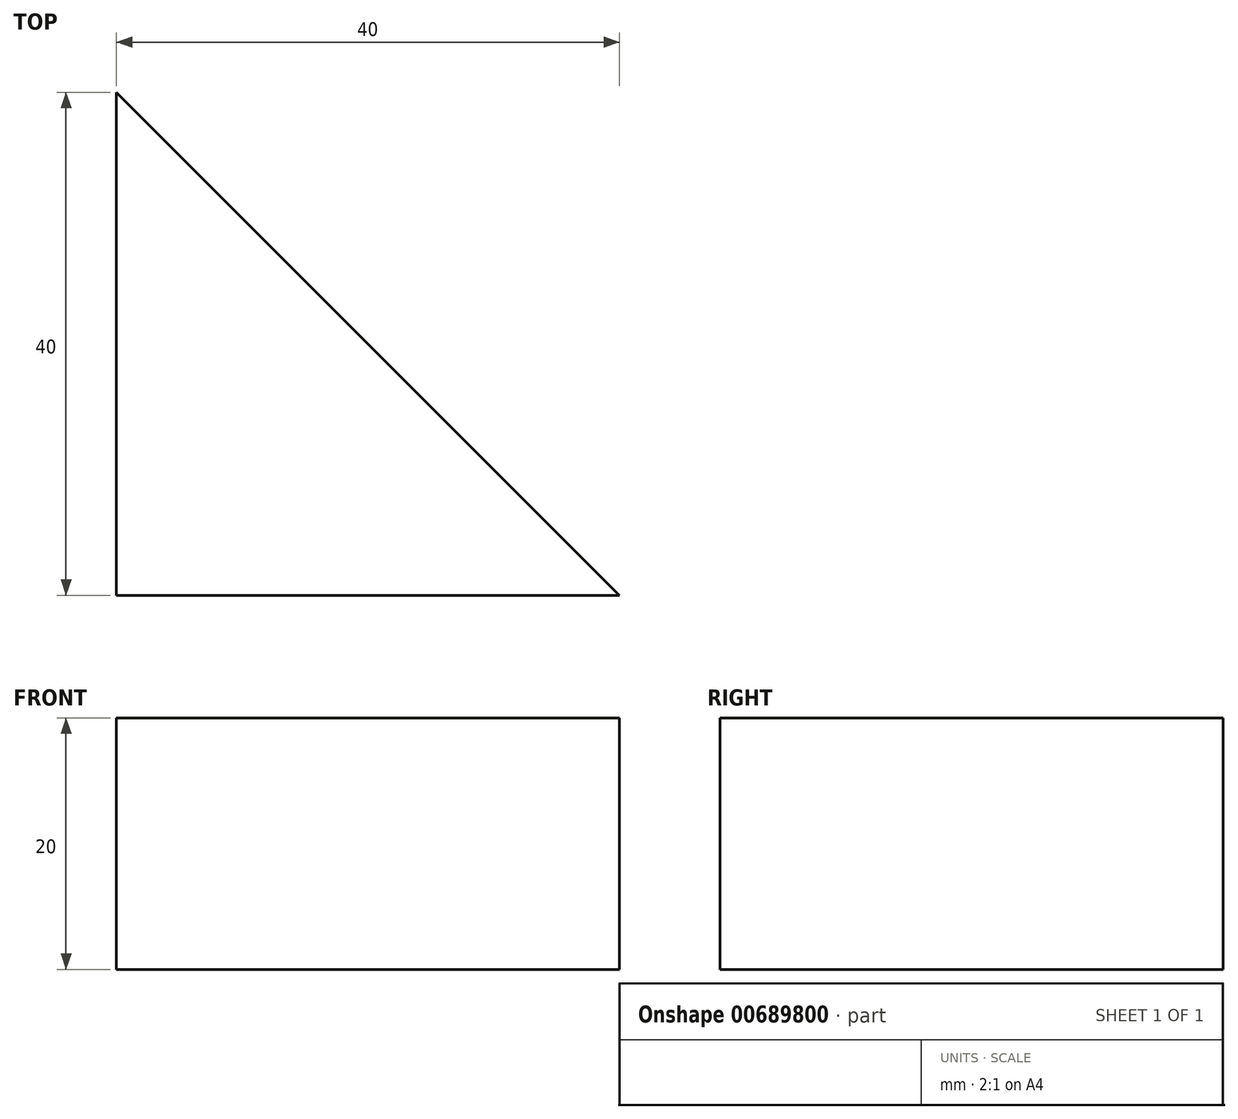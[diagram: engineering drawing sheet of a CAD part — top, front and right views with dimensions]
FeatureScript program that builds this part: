
annotation { "Feature Type Name" : "Feature", "Feature Type Description" : "" }
export const myFeature = defineFeature(function(context is Context, id is Id, definition is map)
    precondition{}
    {
        {
            var Q0;
            Q0=qCreatedBy(makeId("Top.planeOp"),FACE);
            var sketch = newSketch(context, id + "F0", { "sketchPlane" : qUnion([Q0])});
            skLineSegment(sketch, "E0", {"start": v(0, 0) * mm, "end": v(0, 40) * mm});
            skLineSegment(sketch, "E1", {"start": v(0, 40) * mm, "end": v(40, 0) * mm});
            skLineSegment(sketch, "E2", {"start": v(40, 0) * mm, "end": v(0, 0) * mm});
            skSolve(sketch);
        }
        {
            var Q0;
            Q0=makeQuery(id+"F0.imprint","IMPRINT",FACE,{"disambiguationData":[TD([[makeQuery(id+"F0.imprint","IMPRINT",EDGE,{"derivedFrom":sQuery(id+"F0.wireOp",EDGE,"E0")}),-1.0]])]});
            extrude(context, id + "F1", {"entities" : qUnion([Q0]), "depth" : 20 * mm, "offsetDistance" : 25 * mm});
        }
    });
